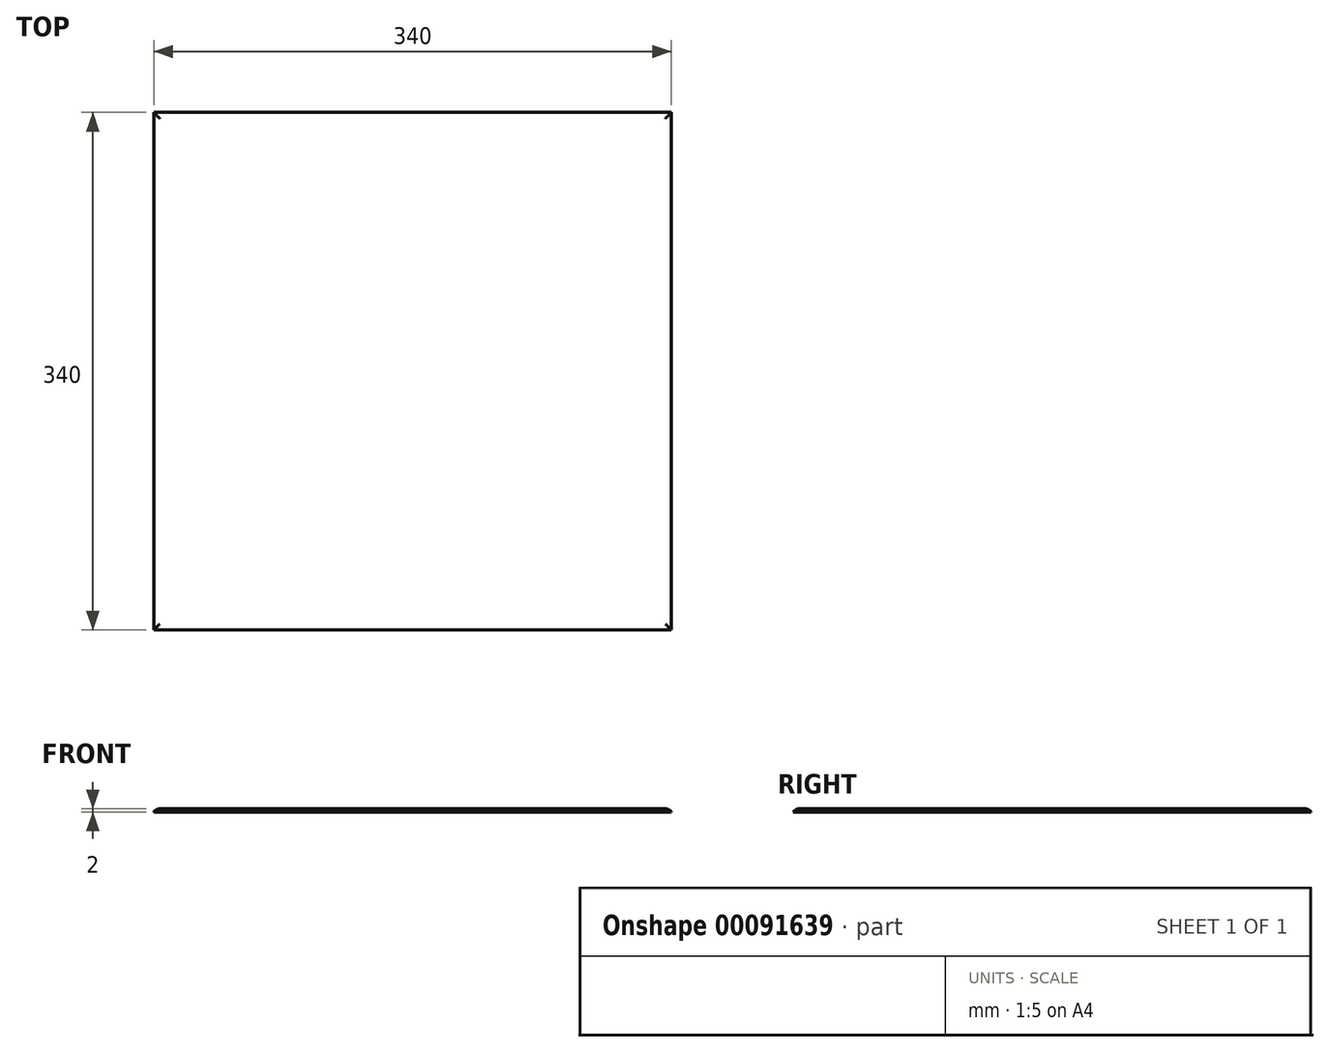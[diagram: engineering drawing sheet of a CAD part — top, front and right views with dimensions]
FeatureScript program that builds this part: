
annotation { "Feature Type Name" : "Feature", "Feature Type Description" : "" }
export const myFeature = defineFeature(function(context is Context, id is Id, definition is map)
    precondition{}
    {
        {
            var Q0;
            Q0=qCreatedBy(makeId("Top.planeOp"),FACE);
            var sketch = newSketch(context, id + "F0", { "sketchPlane" : qUnion([Q0])});
            skLineSegment(sketch, "E0.bottom", {"start": v(170, 170) * mm, "end": v(-170, 170) * mm});
            skLineSegment(sketch, "E0.top", {"start": v(170, -170) * mm, "end": v(-170, -170) * mm});
            skLineSegment(sketch, "E0.left", {"start": v(170, 170) * mm, "end": v(170, -170) * mm});
            skLineSegment(sketch, "E0.right", {"start": v(-170, 170) * mm, "end": v(-170, -170) * mm});
            skPoint(sketch, "E0.middle", {"position": v(0, 0) * mm});
            skPoint(sketch, "E1", {"position": v(157.5, -95) * mm});
            skPoint(sketch, "E2", {"position": v(95, -157.5) * mm});
            skPoint(sketch, "E3", {"position": v(157.5, 95) * mm});
            skPoint(sketch, "E4", {"position": v(95, 157.5) * mm});
            skPoint(sketch, "E5", {"position": v(-95, 157.5) * mm});
            skPoint(sketch, "E6", {"position": v(-157.5, 95) * mm});
            skPoint(sketch, "E7", {"position": v(-157.5, -95) * mm});
            skPoint(sketch, "E8", {"position": v(-95, -157.5) * mm});
            skSolve(sketch);
        }
        {
            var Q0;
            Q0 = qSketchRegion(id + "F0", true);
            extrude(context, id + "F1", {"entities" : qUnion([Q0]), "depth" : 2 * mm});
        }
        {
            var Q0;
            Q0=makeQuery(id+"F1.opExtrude","CAP_EDGE",EDGE,{"disambiguationData":[OSD([sQuery(id+"F0.wireOp",EDGE,"E0.left")])],"isStart":false});
            var Q1;
            Q1=makeQuery(id+"F1.opExtrude","CAP_EDGE",EDGE,{"disambiguationData":[OSD([sQuery(id+"F0.wireOp",EDGE,"E0.top")])],"isStart":false});
            var Q2;
            Q2=makeQuery(id+"F1.opExtrude","CAP_EDGE",EDGE,{"disambiguationData":[OSD([sQuery(id+"F0.wireOp",EDGE,"E0.bottom")])],"isStart":false});
            var Q3;
            Q3=makeQuery(id+"F1.opExtrude","CAP_EDGE",EDGE,{"disambiguationData":[OSD([sQuery(id+"F0.wireOp",EDGE,"E0.right")])],"isStart":false});
            fillet(context, id + "F2", {"entities" : qUnion([Q0, Q1, Q2, Q3]), "radius" : 5 * mm, "tangentPropagation" : true, "allowEdgeOverflow" : false});
        }
    });
